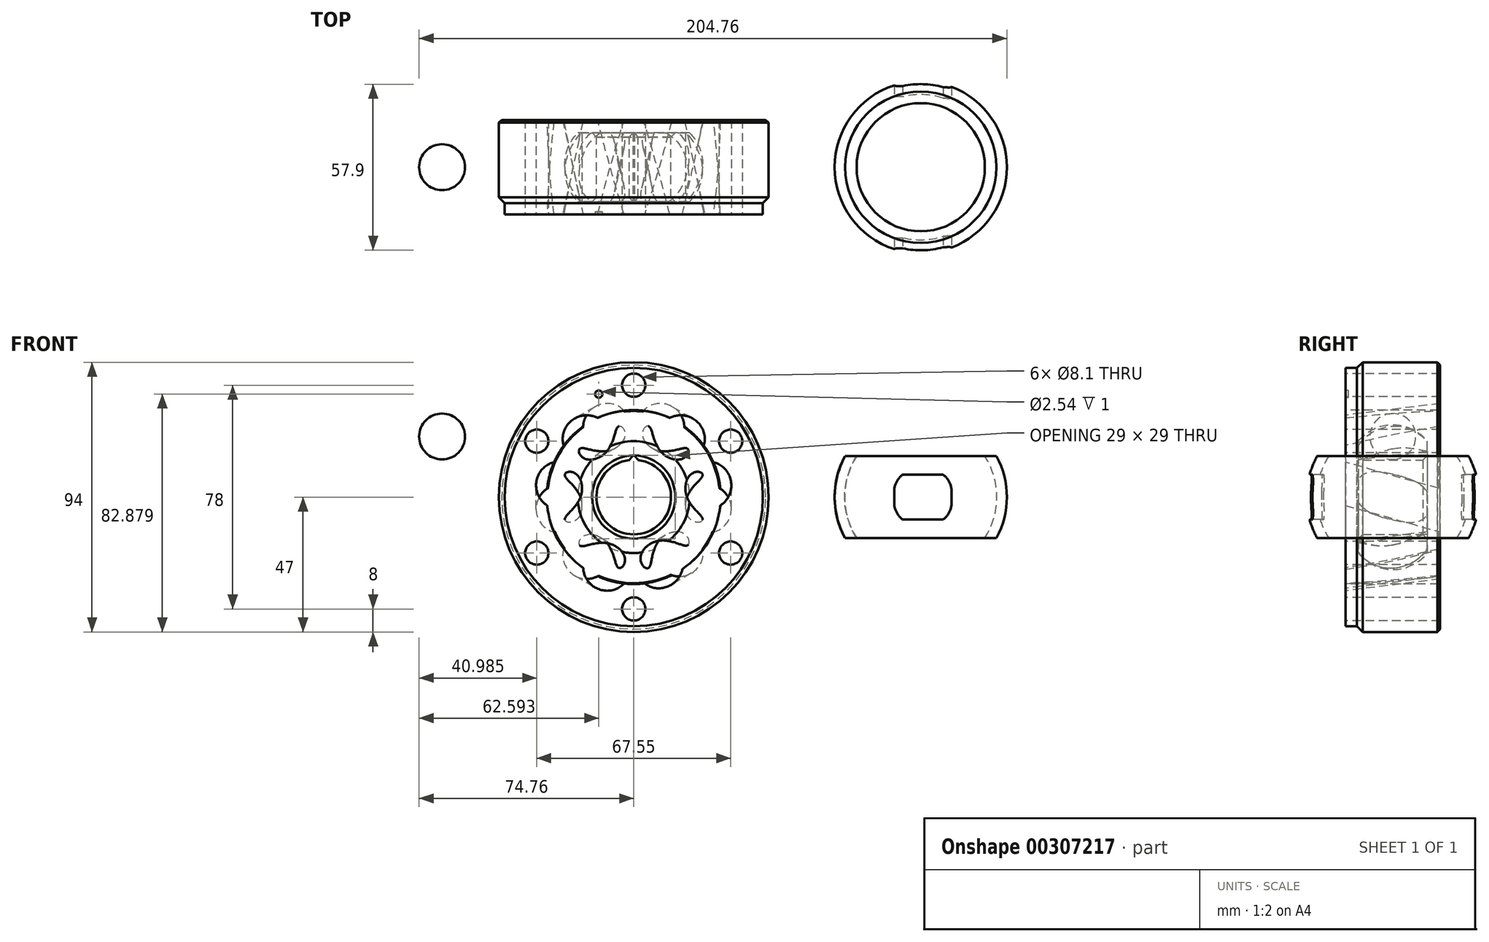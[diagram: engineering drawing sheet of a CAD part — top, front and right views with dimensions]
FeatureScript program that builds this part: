
annotation { "Feature Type Name" : "Feature", "Feature Type Description" : "" }
export const myFeature = defineFeature(function(context is Context, id is Id, definition is map)
    precondition{}
    {
        {
            var Q0;
            Q0=qCreatedBy(makeId("Front.planeOp"),FACE);
            var sketch = newSketch(context, id + "F0", { "sketchPlane" : qUnion([Q0])});
            skCircle(sketch, "E0", {"center": v(0, 0) * mm, "radius": 47 * mm});
            skSolve(sketch);
        }
        {
            var Q0;
            Q0 = qSketchRegion(id + "F0", true);
            extrude(context, id + "F1", {"entities" : qUnion([Q0]), "depth" : 33 * mm, "symmetric" : true});
        }
        {
            var Q0;
            Q0=qCreatedBy(makeId("Front.planeOp"),FACE);
            var sketch = newSketch(context, id + "F2", { "sketchPlane" : qUnion([Q0])});
            skCircle(sketch, "E1", {"center": v(0, 0) * mm, "radius": 39 * mm, "construction": true});
            skCircle(sketch, "E2", {"center": v(0, 39) * mm, "radius": 4.05 * mm});
            skCircle(sketch, "E3.1.1", {"center": v(-33.77, 19.5) * mm, "radius": 4.05 * mm});
            skCircle(sketch, "E3.2.1", {"center": v(-33.77, -19.5) * mm, "radius": 4.05 * mm});
            skCircle(sketch, "E3.3.1", {"center": v(0, -39) * mm, "radius": 4.05 * mm});
            skCircle(sketch, "E3.4.1", {"center": v(33.77, -19.5) * mm, "radius": 4.05 * mm});
            skCircle(sketch, "E3.5.1", {"center": v(33.77, 19.5) * mm, "radius": 4.05 * mm});
            skSolve(sketch);
        }
        {
            var Q0;
            Q0 = qSketchRegion(id + "F2", true);
            extrude(context, id + "F3", {"entities" : qUnion([Q0]), "operationType" : NewBodyOperationType.REMOVE, "oppositeDirection" : true, "depth" : 40 * mm, "symmetric" : true});
        }
        {
            var Q0;
            Q0=makeQuery(id+"F1.opExtrude","CAP_FACE",FACE,{"disambiguationData":[OSD([sQuery(id+"F0.wireOp",EDGE,"E0")])],"isStart":false});
            var sketch = newSketch(context, id + "F4", { "sketchPlane" : qUnion([Q0])});
            skCircle(sketch, "E4", {"center": v(0, 0) * mm, "radius": 30 * mm});
            skSolve(sketch);
        }
        {
            var Q0;
            Q0 = qSketchRegion(id + "F4", true);
            var Q1;
            Q1=makeQuery(id+"F1.opExtrude","CAP_FACE",FACE,{"disambiguationData":[OSD([sQuery(id+"F0.wireOp",EDGE,"E0")])],"isStart":true});
            extrude(context, id + "F5", {"entities" : qUnion([Q0]), "operationType" : NewBodyOperationType.REMOVE, "endBound" : BoundingType.UP_TO_SURFACE, "oppositeDirection" : true, "endBoundEntityFace" : qUnion([Q1]), "depth" : 25 * mm});
        }
        {
            var Q0;
            Q0=makeQuery(id+"F1.opExtrude","CAP_FACE",FACE,{"disambiguationData":[OSD([sQuery(id+"F0.wireOp",EDGE,"E0")])],"isStart":false});
            var sketch = newSketch(context, id + "F6", { "sketchPlane" : qUnion([Q0])});
            skCircle(sketch, "E5", {"center": v(0, 0) * mm, "radius": 45 * mm});
            skCircle(sketch, "E6", {"center": v(0, -1.7) * mm, "radius": 59.4 * mm});
            skSolve(sketch);
        }
        {
            var Q0;
            Q0 = qSketchRegion(id + "F6", true);
            extrude(context, id + "F7", {"entities" : qUnion([Q0]), "operationType" : NewBodyOperationType.REMOVE, "oppositeDirection" : true, "depth" : 6 * mm});
        }
        {
            var Q0;
            Q0=makeQuery(id+"F7.boolean.opBoolean","COPY",EDGE,{"derivedFrom":makeQuery(id+"F7.opExtrude","CAP_EDGE",EDGE,{"disambiguationData":[OSD([sQuery(id+"F6.wireOp",EDGE,"E5")])],"isStart":true})});
            var Q1;
            Q1=makeQuery(id+"F1.opExtrude","CAP_EDGE",EDGE,{"disambiguationData":[OSD([sQuery(id+"F0.wireOp",EDGE,"E0")])],"isStart":true});
            chamfer(context, id + "F8", {"entities" : qUnion([Q0, Q1]), "width" : 1 * mm, "tangentPropagation" : true});
        }
        {
            var Q0;
            Q0=makeQuery(id+"F7.boolean.opBoolean","COPY",EDGE,{"derivedFrom":makeQuery(id+"F7.opExtrude","CAP_EDGE",EDGE,{"disambiguationData":[OSD([sQuery(id+"F6.wireOp",EDGE,"E5")])],"isStart":false})});
            chamfer(context, id + "F9", {"entities" : qUnion([Q0]), "width" : 2 * mm, "tangentPropagation" : true});
        }
        {
            var Q0;
            Q0=qCreatedBy(makeId("Right.planeOp"),FACE);
            cPlane(context, id + "F10", {"entities" : qUnion([Q0]), "cplaneType" : CPlaneType.OFFSET, "offset" : 26 * mm, "width" : 150 * mm, "height" : 150 * mm});
        }
        {
            var Q0;
            Q0=qCreatedBy(id+"F10.planeOp",FACE);
            var sketch = newSketch(context, id + "F11", { "sketchPlane" : qUnion([Q0])});
            skLineSegment(sketch, "E7", {"start": v(45.9, 0) * mm, "end": v(-16.5, 0) * mm, "construction": true});
            skLineSegment(sketch, "E8", {"start": v(0, 0) * mm, "end": v(0, -57.5) * mm, "construction": true});
            skLineSegment(sketch, "E9", {"start": v(-16.5, 4.11) * mm, "end": v(16.5, -4.11) * mm, "construction": true});
            skLineSegment(sketch, "E10", {"start": v(0, 0) * mm, "end": v(-4.76, 1.19) * mm, "construction": true});
            skLineSegment(sketch, "E11", {"start": v(-16.5, 4.11) * mm, "end": v(-23.05, -22.17) * mm});
            skSolve(sketch);
        }
        {
            var Q0;
            Q0=sQuery(id+"F11.wireOp",EDGE,"E11");
            cPlane(context, id + "F12", {"entities" : qUnion([Q0]), "cplaneType" : CPlaneType.LINE_ANGLE, "offset" : 25 * mm, "angle" : 90 * degree, "oppositeDirection" : true, "width" : 150 * mm, "height" : 150 * mm});
        }
        {
            var Q0;
            Q0=qCreatedBy(id+"F12.planeOp",FACE);
            var sketch = newSketch(context, id + "F13", { "sketchPlane" : qUnion([Q0])});
            skCircle(sketch, "E12", {"center": v(26, 0) * mm, "radius": 8 * mm});
            skSolve(sketch);
        }
        {
            var Q0;
            Q0 = qSketchRegion(id + "F13", true);
            var Q1;
            Q1=makeQuery(id+"F1.opExtrude","CAP_FACE",FACE,{"disambiguationData":[OSD([sQuery(id+"F0.wireOp",EDGE,"E0")])],"isStart":true});
            extrude(context, id + "F14", {"entities" : qUnion([Q0]), "operationType" : NewBodyOperationType.REMOVE, "endBound" : BoundingType.UP_TO_SURFACE, "oppositeDirection" : true, "endBoundEntityFace" : qUnion([Q1]), "depth" : 25 * mm, "hasSecondDirection" : true, "secondDirectionOppositeDirection" : false, "secondDirectionDepth" : 25 * mm});
        }
        {
            var Q0;
            Q0=qCreatedBy(makeId("Top.planeOp"),FACE);
            var sketch = newSketch(context, id + "F15", { "sketchPlane" : qUnion([Q0])});
            skLineSegment(sketch, "E13", {"start": v(0, 0) * mm, "end": v(0, -105.8) * mm, "construction": true});
            skSolve(sketch);
        }
        {
            var Q0;
            Q0=sQuery(id+"F15.wireOp",EDGE,"E13");
            var Q1;
            Q1=qCreatedBy(makeId("Right.planeOp"),FACE);
            cPlane(context, id + "F16", {"entities" : qUnion([Q0, Q1]), "cplaneType" : CPlaneType.LINE_ANGLE, "offset" : 25 * mm, "angle" : 60 * degree, "width" : 150 * mm, "height" : 150 * mm});
        }
        {
            var Q0;
            Q0=qCreatedBy(id+"F16.planeOp",FACE);
            cPlane(context, id + "F17", {"entities" : qUnion([Q0]), "cplaneType" : CPlaneType.OFFSET, "offset" : 26 * mm, "width" : 150 * mm, "height" : 150 * mm});
        }
        {
            var Q0;
            Q0=sQuery(id+"F15.wireOp",EDGE,"E13");
            var Q1;
            Q1=qCreatedBy(makeId("Right.planeOp"),FACE);
            cPlane(context, id + "F18", {"entities" : qUnion([Q0, Q1]), "cplaneType" : CPlaneType.LINE_ANGLE, "offset" : 25 * mm, "angle" : 120 * degree, "width" : 150 * mm, "height" : 150 * mm});
        }
        {
            var Q0;
            Q0=qCreatedBy(id+"F18.planeOp",FACE);
            cPlane(context, id + "F19", {"entities" : qUnion([Q0]), "cplaneType" : CPlaneType.OFFSET, "offset" : 26 * mm, "oppositeDirection" : true, "width" : 150 * mm, "height" : 150 * mm});
        }
        {
            var Q0;
            Q0=qCreatedBy(id+"F19.planeOp",FACE);
            var sketch = newSketch(context, id + "F20", { "sketchPlane" : qUnion([Q0])});
            skLineSegment(sketch, "E14", {"start": v(0, 0) * mm, "end": v(0, 13.06) * mm, "construction": true});
            skLineSegment(sketch, "E15", {"start": v(0, 0) * mm, "end": v(-4.11, 16.5) * mm, "construction": true});
            skLineSegment(sketch, "E16", {"start": v(-4.11, 16.5) * mm, "end": v(37.61, 26.9) * mm, "construction": true});
            skSolve(sketch);
        }
        {
            var Q0;
            Q0=sQuery(id+"F20.wireOp",EDGE,"E16");
            var Q1;
            Q1=qCreatedBy(id+"F19.planeOp",FACE);
            cPlane(context, id + "F21", {"entities" : qUnion([Q0, Q1]), "cplaneType" : CPlaneType.LINE_ANGLE, "offset" : 25 * mm, "angle" : 90 * degree, "width" : 150 * mm, "height" : 150 * mm});
        }
        {
            var Q0;
            Q0=qCreatedBy(id+"F21.planeOp",FACE);
            var sketch = newSketch(context, id + "F22", { "sketchPlane" : qUnion([Q0])});
            skCircle(sketch, "E17", {"center": v(-13.3, 22.34) * mm, "radius": 8 * mm});
            skSolve(sketch);
        }
        {
            var Q0;
            Q0 = qSketchRegion(id + "F22", true);
            var Q1;
            Q1=makeQuery(id+"F1.opExtrude","CAP_FACE",FACE,{"disambiguationData":[OSD([sQuery(id+"F0.wireOp",EDGE,"E0")])],"isStart":true});
            var Q2;
            Q2=makeQuery(id+"F1.opExtrude","CAP_FACE",FACE,{"disambiguationData":[OSD([sQuery(id+"F0.wireOp",EDGE,"E0")])],"isStart":true});
            extrude(context, id + "F23", {"entities" : qUnion([Q0]), "operationType" : NewBodyOperationType.REMOVE, "endBound" : BoundingType.UP_TO_SURFACE, "oppositeDirection" : true, "endBoundEntityFace" : qUnion([Q1]), "depth" : 25 * mm, "hasSecondDirection" : true, "secondDirectionOppositeDirection" : false, "secondDirectionBoundEntityFace" : qUnion([Q2]), "secondDirectionDepth" : 25 * mm});
        }
        {
            var Q0;
            Q0=qCreatedBy(id+"F17.planeOp",FACE);
            var sketch = newSketch(context, id + "F24", { "sketchPlane" : qUnion([Q0])});
            skLineSegment(sketch, "E18", {"start": v(0, 0) * mm, "end": v(0, 11.58) * mm, "construction": true});
            skLineSegment(sketch, "E19", {"start": v(0, 0) * mm, "end": v(4.43, 17.75) * mm, "construction": true});
            skLineSegment(sketch, "E20", {"start": v(4.43, 17.75) * mm, "end": v(-28.29, 25.91) * mm, "construction": true});
            skSolve(sketch);
        }
        {
            var Q0;
            Q0=sQuery(id+"F24.wireOp",EDGE,"E20");
            var Q1;
            Q1=qCreatedBy(id+"F17.planeOp",FACE);
            cPlane(context, id + "F25", {"entities" : qUnion([Q0, Q1]), "cplaneType" : CPlaneType.LINE_ANGLE, "offset" : 25 * mm, "angle" : 90 * degree, "width" : 150 * mm, "height" : 150 * mm});
        }
        {
            var Q0;
            Q0=qCreatedBy(id+"F25.planeOp",FACE);
            var sketch = newSketch(context, id + "F26", { "sketchPlane" : qUnion([Q0])});
            skCircle(sketch, "E21", {"center": v(13.3, -22.34) * mm, "radius": 8 * mm});
            skSolve(sketch);
        }
        {
            var Q0;
            Q0 = qSketchRegion(id + "F26", true);
            var Q1;
            Q1=makeQuery(id+"F1.opExtrude","CAP_FACE",FACE,{"disambiguationData":[OSD([sQuery(id+"F0.wireOp",EDGE,"E0")])],"isStart":true});
            extrude(context, id + "F27", {"entities" : qUnion([Q0]), "operationType" : NewBodyOperationType.REMOVE, "endBound" : BoundingType.UP_TO_SURFACE, "endBoundEntityFace" : qUnion([Q1]), "depth" : 25 * mm, "hasSecondDirection" : true, "secondDirectionOppositeDirection" : true, "secondDirectionDepth" : 25 * mm});
        }
        {
            var Q0;
            Q0=qCreatedBy(makeId("Top.planeOp"),FACE);
            var Q1;
            Q1=sQuery(id+"F15.wireOp",EDGE,"E13");
            cPlane(context, id + "F28", {"entities" : qUnion([Q0, Q1]), "cplaneType" : CPlaneType.LINE_ANGLE, "offset" : 25 * mm, "angle" : 330 * degree, "width" : 150 * mm, "height" : 150 * mm});
        }
        {
            var Q0;
            Q0=qCreatedBy(id+"F28.planeOp",FACE);
            cPlane(context, id + "F29", {"entities" : qUnion([Q0]), "cplaneType" : CPlaneType.OFFSET, "offset" : 26 * mm, "oppositeDirection" : true, "width" : 150 * mm, "height" : 150 * mm});
        }
        {
            var Q0;
            Q0=qCreatedBy(id+"F29.planeOp",FACE);
            var sketch = newSketch(context, id + "F30", { "sketchPlane" : qUnion([Q0])});
            skLineSegment(sketch, "E22", {"start": v(0, 0) * mm, "end": v(0, 16.49) * mm, "construction": true});
            skLineSegment(sketch, "E23", {"start": v(0, 0) * mm, "end": v(4.76, 19.08) * mm, "construction": true});
            skLineSegment(sketch, "E24", {"start": v(4.76, 19.08) * mm, "end": v(-15.36, 24.1) * mm, "construction": true});
            skSolve(sketch);
        }
        {
            var Q0;
            Q0=sQuery(id+"F30.wireOp",EDGE,"E24");
            var Q1;
            Q1=qCreatedBy(id+"F29.planeOp",FACE);
            cPlane(context, id + "F31", {"entities" : qUnion([Q0, Q1]), "cplaneType" : CPlaneType.LINE_ANGLE, "offset" : 25 * mm, "angle" : 90 * degree, "width" : 150 * mm, "height" : 150 * mm});
        }
        {
            var Q0;
            Q0=qCreatedBy(id+"F31.planeOp",FACE);
            var sketch = newSketch(context, id + "F32", { "sketchPlane" : qUnion([Q0])});
            skCircle(sketch, "E25", {"center": v(-13.3, 22.34) * mm, "radius": 8 * mm});
            skSolve(sketch);
        }
        {
            var Q0;
            Q0 = qSketchRegion(id + "F32", true);
            var Q1;
            Q1=makeQuery(id+"F1.opExtrude","CAP_FACE",FACE,{"disambiguationData":[OSD([sQuery(id+"F0.wireOp",EDGE,"E0")])],"isStart":true});
            extrude(context, id + "F33", {"entities" : qUnion([Q0]), "operationType" : NewBodyOperationType.REMOVE, "endBound" : BoundingType.UP_TO_SURFACE, "endBoundEntityFace" : qUnion([Q1]), "depth" : 25 * mm});
        }
        {
            var Q0;
            Q0=sQuery(id+"F15.wireOp",EDGE,"E13");
            var Q1;
            Q1=qCreatedBy(id+"F28.planeOp",FACE);
            cPlane(context, id + "F34", {"entities" : qUnion([Q0, Q1]), "cplaneType" : CPlaneType.LINE_ANGLE, "offset" : 25 * mm, "angle" : 120 * degree, "width" : 150 * mm, "height" : 150 * mm});
        }
        {
            var Q0;
            Q0=qCreatedBy(id+"F34.planeOp",FACE);
            cPlane(context, id + "F35", {"entities" : qUnion([Q0]), "cplaneType" : CPlaneType.OFFSET, "offset" : 26 * mm, "width" : 150 * mm, "height" : 150 * mm});
        }
        {
            var Q0;
            Q0=qCreatedBy(id+"F35.planeOp",FACE);
            var sketch = newSketch(context, id + "F36", { "sketchPlane" : qUnion([Q0])});
            skLineSegment(sketch, "E26", {"start": v(0, 0) * mm, "end": v(13.95, 0) * mm, "construction": true});
            skLineSegment(sketch, "E27", {"start": v(0, 0) * mm, "end": v(16.5, 4.11) * mm, "construction": true});
            skLineSegment(sketch, "E28", {"start": v(16.5, 4.11) * mm, "end": v(20.29, -11.07) * mm, "construction": true});
            skSolve(sketch);
        }
        {
            var Q0;
            Q0=sQuery(id+"F36.wireOp",EDGE,"E28");
            var Q1;
            Q1=qCreatedBy(id+"F35.planeOp",FACE);
            cPlane(context, id + "F37", {"entities" : qUnion([Q0, Q1]), "cplaneType" : CPlaneType.LINE_ANGLE, "offset" : 25 * mm, "angle" : 90 * degree, "width" : 150 * mm, "height" : 150 * mm});
        }
        {
            var Q0;
            Q0=qCreatedBy(id+"F37.planeOp",FACE);
            var sketch = newSketch(context, id + "F38", { "sketchPlane" : qUnion([Q0])});
            skCircle(sketch, "E29", {"center": v(-26, 0) * mm, "radius": 8 * mm});
            skSolve(sketch);
        }
        {
            var Q0;
            Q0 = qSketchRegion(id + "F38", true);
            var Q1;
            Q1=makeQuery(id+"F1.opExtrude","CAP_FACE",FACE,{"disambiguationData":[OSD([sQuery(id+"F0.wireOp",EDGE,"E0")])],"isStart":true});
            extrude(context, id + "F39", {"entities" : qUnion([Q0]), "operationType" : NewBodyOperationType.REMOVE, "endBound" : BoundingType.UP_TO_SURFACE, "oppositeDirection" : true, "endBoundEntityFace" : qUnion([Q1]), "depth" : 25 * mm, "hasSecondDirection" : true, "secondDirectionOppositeDirection" : false, "secondDirectionDepth" : 25 * mm});
        }
        {
            var Q0;
            Q0=qCreatedBy(id+"F34.planeOp",FACE);
            var Q1;
            Q1=sQuery(id+"F15.wireOp",EDGE,"E13");
            cPlane(context, id + "F40", {"entities" : qUnion([Q0, Q1]), "cplaneType" : CPlaneType.LINE_ANGLE, "offset" : 25 * mm, "angle" : 120 * degree, "width" : 150 * mm, "height" : 150 * mm});
        }
        {
            var Q0;
            Q0=qCreatedBy(id+"F40.planeOp",FACE);
            cPlane(context, id + "F41", {"entities" : qUnion([Q0]), "cplaneType" : CPlaneType.OFFSET, "offset" : 25 * mm, "oppositeDirection" : true, "width" : 150 * mm, "height" : 150 * mm});
        }
        {
            var Q0;
            Q0=qCreatedBy(id+"F41.planeOp",FACE);
            var sketch = newSketch(context, id + "F42", { "sketchPlane" : qUnion([Q0])});
            skLineSegment(sketch, "E30", {"start": v(0, 0) * mm, "end": v(0, -15.94) * mm, "construction": true});
            skLineSegment(sketch, "E31", {"start": v(0, 0) * mm, "end": v(-4.11, -16.5) * mm, "construction": true});
            skLineSegment(sketch, "E32", {"start": v(-4.11, -16.5) * mm, "end": v(10.82, -20.22) * mm, "construction": true});
            skSolve(sketch);
        }
        {
            var Q0;
            Q0=sQuery(id+"F42.wireOp",EDGE,"E32");
            var Q1;
            Q1=qCreatedBy(id+"F41.planeOp",FACE);
            cPlane(context, id + "F43", {"entities" : qUnion([Q0, Q1]), "cplaneType" : CPlaneType.LINE_ANGLE, "offset" : 25 * mm, "angle" : 90 * degree, "width" : 150 * mm, "height" : 150 * mm});
        }
        {
            var Q0;
            Q0=qCreatedBy(id+"F43.planeOp",FACE);
            var sketch = newSketch(context, id + "F44", { "sketchPlane" : qUnion([Q0])});
            skCircle(sketch, "E33", {"center": v(-12.78, -21.48) * mm, "radius": 8 * mm});
            skSolve(sketch);
        }
        {
            var Q0;
            Q0 = qSketchRegion(id + "F44", true);
            var Q1;
            Q1=makeQuery(id+"F1.opExtrude","CAP_FACE",FACE,{"disambiguationData":[OSD([sQuery(id+"F0.wireOp",EDGE,"E0")])],"isStart":true});
            extrude(context, id + "F45", {"entities" : qUnion([Q0]), "operationType" : NewBodyOperationType.REMOVE, "endBound" : BoundingType.UP_TO_SURFACE, "endBoundEntityFace" : qUnion([Q1]), "depth" : 25 * mm, "hasSecondDirection" : true, "secondDirectionOppositeDirection" : true, "secondDirectionDepth" : 25 * mm});
        }
        {
            var Q0;
            Q0=qCreatedBy(makeId("Front.planeOp"),FACE);
            var sketch = newSketch(context, id + "F46", { "sketchPlane" : qUnion([Q0])});
            skArc(sketch, "E34", {"start": v(-66.76, 29.11) * mm, "mid": v(-74.76, 21.11) * mm, "end": v(-66.76, 13.11) * mm});
            skLineSegment(sketch, "E35", {"start": v(-66.76, 29.11) * mm, "end": v(-66.76, 13.11) * mm});
            skLineSegment(sketch, "E36", {"start": v(-66.76, 42.78) * mm, "end": v(-66.76, -5.2) * mm, "construction": true});
            skSolve(sketch);
        }
        {
            var Q0;
            Q0 = qSketchRegion(id + "F46", true);
            var Q1;
            Q1=sQuery(id+"F46.wireOp",EDGE,"E35");
            revolve(context, id + "F47", {"entities" : qUnion([Q0]), "axis" : qUnion([Q1]), "revolveType" : RevolveType.FULL});
        }
        {
            var Q0;
            Q0=qCreatedBy(makeId("Right.planeOp"),FACE);
            cPlane(context, id + "F48", {"entities" : qUnion([Q0]), "cplaneType" : CPlaneType.OFFSET, "offset" : 100 * mm, "width" : 150 * mm, "height" : 150 * mm});
        }
        {
            var Q0;
            Q0=qCreatedBy(makeId("Front.planeOp"),FACE);
            var sketch = newSketch(context, id + "F49", { "sketchPlane" : qUnion([Q0])});
            skArc(sketch, "E37", {"start": v(100, -30) * mm, "mid": v(130, 0) * mm, "end": v(100, 30) * mm});
            skLineSegment(sketch, "E38", {"start": v(100, 30) * mm, "end": v(100, -30) * mm});
            skSolve(sketch);
        }
        {
            var Q0;
            Q0 = qSketchRegion(id + "F49", true);
            var Q1;
            Q1=sQuery(id+"F49.wireOp",EDGE,"E38");
            revolve(context, id + "F50", {"entities" : qUnion([Q0]), "axis" : qUnion([Q1]), "revolveType" : RevolveType.FULL});
        }
        {
            var Q0;
            Q0=qCreatedBy(makeId("Front.planeOp"),FACE);
            var sketch = newSketch(context, id + "F51", { "sketchPlane" : qUnion([Q0])});
            skLineSegment(sketch, "E39", {"start": v(65.97, 0) * mm, "end": v(144.14, 0) * mm, "construction": true});
            skLineSegment(sketch, "E40.bottom", {"start": v(66.97, -14.25) * mm, "end": v(140.64, -14.25) * mm});
            skLineSegment(sketch, "E40.top", {"start": v(66.97, -42.47) * mm, "end": v(140.64, -42.47) * mm});
            skLineSegment(sketch, "E40.left", {"start": v(66.97, -14.25) * mm, "end": v(66.97, -42.47) * mm});
            skLineSegment(sketch, "E40.right", {"start": v(140.64, -14.25) * mm, "end": v(140.64, -42.47) * mm});
            skLineSegment(sketch, "E41.bottom", {"start": v(66.97, 14.25) * mm, "end": v(140.64, 14.25) * mm});
            skLineSegment(sketch, "E41.top", {"start": v(66.97, 36.05) * mm, "end": v(140.64, 36.05) * mm});
            skLineSegment(sketch, "E41.left", {"start": v(66.97, 14.25) * mm, "end": v(66.97, 36.05) * mm});
            skLineSegment(sketch, "E41.right", {"start": v(140.64, 14.25) * mm, "end": v(140.64, 36.05) * mm});
            skSolve(sketch);
        }
        {
            var Q0;
            Q0 = qSketchRegion(id + "F51", true);
            extrude(context, id + "F52", {"entities" : qUnion([Q0]), "operationType" : NewBodyOperationType.REMOVE, "oppositeDirection" : true, "depth" : 100 * mm, "symmetric" : true});
        }
        {
            var Q0;
            Q0=makeQuery(id+"F52.boolean.opBoolean","COPY",FACE,{"derivedFrom":makeQuery(id+"F52.opExtrude","SWEPT_FACE",FACE,{"disambiguationData":[OSD([sQuery(id+"F51.wireOp",EDGE,"E41.bottom")])]})});
            var Q1;
            Q1=makeQuery(id+"F52.boolean.opBoolean","COPY",FACE,{"derivedFrom":makeQuery(id+"F52.opExtrude","SWEPT_FACE",FACE,{"disambiguationData":[OSD([sQuery(id+"F51.wireOp",EDGE,"E40.bottom")])]})});
            shell(context, id + "F53", {"entities" : qUnion([Q0, Q1]), "thickness" : 3.5 * mm});
        }
        {
            var Q0;
            Q0=qCreatedBy(makeId("Front.planeOp"),FACE);
            var sketch = newSketch(context, id + "F54", { "sketchPlane" : qUnion([Q0])});
            skLineSegment(sketch, "E42.bottom", {"start": v(107.75, -7.85) * mm, "end": v(93.75, -7.85) * mm});
            skLineSegment(sketch, "E42.top", {"start": v(107.75, 7.85) * mm, "end": v(93.75, 7.85) * mm});
            skLineSegment(sketch, "E42.left", {"start": v(110.75, -2) * mm, "end": v(110.75, 2) * mm});
            skLineSegment(sketch, "E42.right", {"start": v(90.75, -2) * mm, "end": v(90.75, 2) * mm});
            skPoint(sketch, "E42.middle", {"position": v(100.75, 0) * mm});
            skPoint(sketch, "E43.middle", {"position": v(99.82, -11.86) * mm});
            skLineSegment(sketch, "E44", {"start": v(93.75, 7.85) * mm, "end": v(93.75, -7.85) * mm, "construction": true});
            skLineSegment(sketch, "E45", {"start": v(107.75, 7.85) * mm, "end": v(107.75, -7.85) * mm, "construction": true});
            skLineSegment(sketch, "E46", {"start": v(90.75, 2) * mm, "end": v(110.75, 2) * mm, "construction": true});
            skLineSegment(sketch, "E47", {"start": v(110.75, -2) * mm, "end": v(90.75, -2) * mm, "construction": true});
            skLineSegment(sketch, "E48", {"start": v(100.75, 0) * mm, "end": v(103.88, 0) * mm, "construction": true});
            skArc(sketch, "E49", {"start": v(110.75, 2) * mm, "mid": v(109.96, 5.29) * mm, "end": v(107.75, 7.85) * mm});
            skArc(sketch, "E50", {"start": v(107.75, -7.85) * mm, "mid": v(109.96, -5.29) * mm, "end": v(110.75, -2) * mm});
            skArc(sketch, "E51", {"start": v(90.75, -2) * mm, "mid": v(91.55, -5.29) * mm, "end": v(93.75, -7.85) * mm});
            skArc(sketch, "E52", {"start": v(93.75, 7.85) * mm, "mid": v(91.55, 5.29) * mm, "end": v(90.75, 2) * mm});
            skPoint(sketch, "E53.orphan", {"position": v(90.75, 7.85) * mm});
            skPoint(sketch, "E54.orphan", {"position": v(90.75, -7.85) * mm});
            skPoint(sketch, "E55.orphan", {"position": v(110.75, -7.85) * mm});
            skPoint(sketch, "E56.orphan", {"position": v(110.75, 7.85) * mm});
            skSolve(sketch);
        }
        {
            var Q0;
            Q0 = qSketchRegion(id + "F54", true);
            extrude(context, id + "F55", {"entities" : qUnion([Q0]), "operationType" : NewBodyOperationType.REMOVE, "oppositeDirection" : true, "depth" : 70 * mm, "symmetric" : true});
        }
        {
            var Q0;
            Q0=qCreatedBy(makeId("Front.planeOp"),FACE);
            var sketch = newSketch(context, id + "F56", { "sketchPlane" : qUnion([Q0])});
            skCircle(sketch, "E57", {"center": v(0, 0) * mm, "radius": 25.25 * mm});
            skCircle(sketch, "E58", {"center": v(0, 0) * mm, "radius": 14.5 * mm, "construction": true});
            skCircle(sketch, "E59", {"center": v(0, 0) * mm, "radius": 13 * mm});
            skSolve(sketch);
        }
        {
            var Q0;
            Q0 = qSketchRegion(id + "F56", true);
            extrude(context, id + "F57", {"entities" : qUnion([Q0]), "depth" : 24 * mm, "symmetric" : true});
        }
        {
            var Q0;
            Q0=qCreatedBy(id+"F10.planeOp",FACE);
            var sketch = newSketch(context, id + "F58", { "sketchPlane" : qUnion([Q0])});
            skLineSegment(sketch, "E60", {"start": v(0, 0) * mm, "end": v(-16.5, 0) * mm});
            skLineSegment(sketch, "E61", {"start": v(0, 0) * mm, "end": v(-16.5, 4.11) * mm});
            skSolve(sketch);
        }
        {
            var Q0;
            Q0=qCreatedBy(id+"F12.planeOp",FACE);
            var sketch = newSketch(context, id + "F59", { "sketchPlane" : qUnion([Q0])});
            skCircle(sketch, "E62", {"center": v(26, 0) * mm, "radius": 8 * mm});
            skSolve(sketch);
        }
        {
            var Q0;
            Q0 = qSketchRegion(id + "F59", true);
            var Q1;
            Q1=makeQuery(id+"F57.opExtrude","CAP_FACE",FACE,{"disambiguationData":[OSD([sQuery(id+"F56.wireOp",EDGE,"E57"),sQuery(id+"F56.wireOp",EDGE,"E58")])],"isStart":true});
            extrude(context, id + "F60", {"entities" : qUnion([Q0]), "operationType" : NewBodyOperationType.REMOVE, "endBound" : BoundingType.UP_TO_SURFACE, "oppositeDirection" : true, "endBoundEntityFace" : qUnion([Q1]), "depth" : 25 * mm});
        }
        {
            var Q0;
            Q0=qCreatedBy(id+"F19.planeOp",FACE);
            var sketch = newSketch(context, id + "F61", { "sketchPlane" : qUnion([Q0])});
            skLineSegment(sketch, "E63", {"start": v(0, 0) * mm, "end": v(0, 7.15) * mm});
            skLineSegment(sketch, "E64", {"start": v(0, 0) * mm, "end": v(-4.11, 16.5) * mm});
            skSolve(sketch);
        }
        {
            var Q0;
            Q0=qCreatedBy(id+"F21.planeOp",FACE);
            var sketch = newSketch(context, id + "F62", { "sketchPlane" : qUnion([Q0])});
            skCircle(sketch, "E65", {"center": v(-13.3, 22.34) * mm, "radius": 8 * mm});
            skSolve(sketch);
        }
        {
            var Q0;
            Q0 = qSketchRegion(id + "F62", true);
            var Q1;
            Q1=makeQuery(id+"F57.opExtrude","CAP_FACE",FACE,{"disambiguationData":[OSD([sQuery(id+"F56.wireOp",EDGE,"E57"),sQuery(id+"F56.wireOp",EDGE,"E58")])],"isStart":true});
            extrude(context, id + "F63", {"entities" : qUnion([Q0]), "operationType" : NewBodyOperationType.REMOVE, "endBound" : BoundingType.UP_TO_SURFACE, "oppositeDirection" : true, "endBoundEntityFace" : qUnion([Q1]), "depth" : 25 * mm});
        }
        {
            var Q0;
            Q0=qCreatedBy(id+"F17.planeOp",FACE);
            var sketch = newSketch(context, id + "F64", { "sketchPlane" : qUnion([Q0])});
            skLineSegment(sketch, "E66", {"start": v(0, 0) * mm, "end": v(0, 9.52) * mm});
            skLineSegment(sketch, "E67", {"start": v(0, 0) * mm, "end": v(4.43, 17.75) * mm});
            skSolve(sketch);
        }
        {
            var Q0;
            Q0=qCreatedBy(id+"F25.planeOp",FACE);
            var sketch = newSketch(context, id + "F65", { "sketchPlane" : qUnion([Q0])});
            skCircle(sketch, "E68", {"center": v(13.3, -22.34) * mm, "radius": 8 * mm});
            skSolve(sketch);
        }
        {
            var Q0;
            Q0=qCreatedBy(id+"F29.planeOp",FACE);
            var sketch = newSketch(context, id + "F66", { "sketchPlane" : qUnion([Q0])});
            skLineSegment(sketch, "E69", {"start": v(0, 0) * mm, "end": v(0, 7.14) * mm});
            skLineSegment(sketch, "E70", {"start": v(0, 0) * mm, "end": v(4.76, 19.08) * mm});
            skSolve(sketch);
        }
        {
            var Q0;
            Q0=qCreatedBy(id+"F31.planeOp",FACE);
            var sketch = newSketch(context, id + "F67", { "sketchPlane" : qUnion([Q0])});
            skCircle(sketch, "E71", {"center": v(-13.3, 22.34) * mm, "radius": 8 * mm});
            skSolve(sketch);
        }
        {
            var Q0;
            Q0 = qSketchRegion(id + "F67", true);
            var Q1;
            Q1=makeQuery(id+"F57.opExtrude","CAP_FACE",FACE,{"disambiguationData":[OSD([sQuery(id+"F56.wireOp",EDGE,"E57"),sQuery(id+"F56.wireOp",EDGE,"E58")])],"isStart":true});
            extrude(context, id + "F68", {"entities" : qUnion([Q0]), "operationType" : NewBodyOperationType.REMOVE, "endBound" : BoundingType.UP_TO_SURFACE, "endBoundEntityFace" : qUnion([Q1]), "depth" : 25 * mm});
        }
        {
            var Q0;
            Q0=qCreatedBy(id+"F35.planeOp",FACE);
            var sketch = newSketch(context, id + "F69", { "sketchPlane" : qUnion([Q0])});
            skLineSegment(sketch, "E72", {"start": v(0, 0) * mm, "end": v(9.7, 0) * mm});
            skLineSegment(sketch, "E73", {"start": v(0, 0) * mm, "end": v(16.5, 4.11) * mm});
            skSolve(sketch);
        }
        {
            var Q0;
            Q0=qCreatedBy(id+"F37.planeOp",FACE);
            var sketch = newSketch(context, id + "F70", { "sketchPlane" : qUnion([Q0])});
            skCircle(sketch, "E74", {"center": v(-26, 0) * mm, "radius": 8 * mm});
            skSolve(sketch);
        }
        {
            var Q0;
            Q0 = qSketchRegion(id + "F70", true);
            var Q1;
            Q1=makeQuery(id+"F57.opExtrude","CAP_FACE",FACE,{"disambiguationData":[OSD([sQuery(id+"F56.wireOp",EDGE,"E57"),sQuery(id+"F56.wireOp",EDGE,"E58")])],"isStart":true});
            extrude(context, id + "F71", {"entities" : qUnion([Q0]), "operationType" : NewBodyOperationType.REMOVE, "endBound" : BoundingType.UP_TO_SURFACE, "oppositeDirection" : true, "endBoundEntityFace" : qUnion([Q1]), "depth" : 25 * mm});
        }
        {
            var Q0;
            Q0=qCreatedBy(id+"F41.planeOp",FACE);
            var sketch = newSketch(context, id + "F72", { "sketchPlane" : qUnion([Q0])});
            skLineSegment(sketch, "E75", {"start": v(0, 0) * mm, "end": v(0, -9.09) * mm});
            skLineSegment(sketch, "E76", {"start": v(0, 0) * mm, "end": v(-4.11, -16.5) * mm});
            skSolve(sketch);
        }
        {
            var Q0;
            Q0=qCreatedBy(id+"F43.planeOp",FACE);
            var sketch = newSketch(context, id + "F73", { "sketchPlane" : qUnion([Q0])});
            skCircle(sketch, "E77", {"center": v(-12.78, -21.48) * mm, "radius": 8 * mm});
            skSolve(sketch);
        }
        {
            var Q0;
            Q0 = qSketchRegion(id + "F73", true);
            var Q1;
            Q1=makeQuery(id+"F57.opExtrude","CAP_FACE",FACE,{"disambiguationData":[OSD([sQuery(id+"F56.wireOp",EDGE,"E57"),sQuery(id+"F56.wireOp",EDGE,"E58")])],"isStart":true});
            extrude(context, id + "F74", {"entities" : qUnion([Q0]), "operationType" : NewBodyOperationType.REMOVE, "endBound" : BoundingType.UP_TO_SURFACE, "endBoundEntityFace" : qUnion([Q1]), "depth" : 25 * mm});
        }
        {
            var Q0;
            Q0=qCreatedBy(makeId("Top.planeOp"),FACE);
            var sketch = newSketch(context, id + "F75", { "sketchPlane" : qUnion([Q0])});
            skLineSegment(sketch, "E78", {"start": v(0, 0) * mm, "end": v(40.15, 0) * mm, "construction": true});
            skLineSegment(sketch, "E79", {"start": v(0, 0) * mm, "end": v(0, -30.92) * mm, "construction": true});
            skArc(sketch, "E80", {"start": v(-19.5, 12) * mm, "mid": v(-23.73, 6.65) * mm, "end": v(-25.25, 0) * mm});
            skArc(sketch, "E81", {"start": v(-25.25, 0) * mm, "mid": v(-23.73, -6.65) * mm, "end": v(-19.5, -12) * mm});
            skLineSegment(sketch, "E82", {"start": v(-30.3, 15.96) * mm, "end": v(-30.3, -19.54) * mm});
            skLineSegment(sketch, "E83", {"start": v(-30.3, -19.54) * mm, "end": v(-19.5, -12) * mm});
            skLineSegment(sketch, "E84", {"start": v(-19.5, 12) * mm, "end": v(-30.3, 15.96) * mm});
            skSolve(sketch);
        }
        {
            var Q0;
            Q0=makeQuery(id+"F1.opExtrude","CAP_FACE",FACE,{"disambiguationData":[OSD([sQuery(id+"F0.wireOp",EDGE,"E0")])],"isStart":false});
            var sketch = newSketch(context, id + "F76", { "sketchPlane" : qUnion([Q0])});
            skCircle(sketch, "E85", {"center": v(-12.17, 35.88) * mm, "radius": 1.27 * mm});
            skSolve(sketch);
        }
        {
            var Q0;
            Q0 = qSketchRegion(id + "F76", true);
            extrude(context, id + "F77", {"entities" : qUnion([Q0]), "operationType" : NewBodyOperationType.REMOVE, "oppositeDirection" : true, "depth" : 1 * mm});
        }
        {
            var Q0;
            Q0=makeQuery(id+"F57.opExtrude","CAP_FACE",FACE,{"disambiguationData":[OSD([sQuery(id+"F56.wireOp",EDGE,"E57"),sQuery(id+"F56.wireOp",EDGE,"E58")])],"isStart":false});
            var sketch = newSketch(context, id + "F78", { "sketchPlane" : qUnion([Q0])});
            skCircle(sketch, "E86", {"center": v(-4.57, 21.78) * mm, "radius": 1.43 * mm});
            skSolve(sketch);
        }
        {
            var Q0;
            Q0 = qSketchRegion(id + "F78", true);
            extrude(context, id + "F79", {"entities" : qUnion([Q0]), "operationType" : NewBodyOperationType.REMOVE, "oppositeDirection" : true, "depth" : 1 * mm});
        }
        {
            var Q0;
            Q0 = qSketchRegion(id + "F65", true);
            var Q1;
            Q1=makeQuery(id+"F57.opExtrude","CAP_FACE",FACE,{"disambiguationData":[OSD([sQuery(id+"F56.wireOp",EDGE,"E57"),sQuery(id+"F56.wireOp",EDGE,"E58")])],"isStart":true});
            extrude(context, id + "F80", {"entities" : qUnion([Q0]), "operationType" : NewBodyOperationType.REMOVE, "endBound" : BoundingType.UP_TO_SURFACE, "endBoundEntityFace" : qUnion([Q1]), "depth" : 25 * mm});
        }
        {
            var Q0;
            Q0 = qSketchRegion(id + "F75", true);
            var Q1;
            Q1=sQuery(id+"F75.wireOp",EDGE,"E79");
            revolve(context, id + "F81", {"operationType" : NewBodyOperationType.REMOVE, "entities" : qUnion([Q0]), "axis" : qUnion([Q1]), "revolveType" : RevolveType.FULL, "oppositeDirection" : true});
        }
        {
            var Q0;
            Q0=makeQuery(id+"F57.opExtrude","SWEPT_FACE",FACE,{"disambiguationData":[OSD([sQuery(id+"F56.wireOp",EDGE,"E59")])]});
            chamfer(context, id + "F82", {"entities" : qUnion([Q0]), "width" : 1.5 * mm, "tangentPropagation" : true});
        }
        {
            var Q0;
            Q0=makeQuery(id+"F57.opExtrude","CAP_FACE",FACE,{"disambiguationData":[OSD([sQuery(id+"F56.wireOp",EDGE,"E57"),sQuery(id+"F56.wireOp",EDGE,"E59")])],"isStart":false});
            var sketch = newSketch(context, id + "F83", { "sketchPlane" : qUnion([Q0])});
            skLineSegment(sketch, "E87", {"start": v(0, 14.5) * mm, "end": v(0, 12.8) * mm, "construction": true});
            skLineSegment(sketch, "E88", {"start": v(0, 12.8) * mm, "end": v(1.65, 12.8) * mm});
            skLineSegment(sketch, "E89", {"start": v(1.65, 12.8) * mm, "end": v(0.25, 14.5) * mm});
            skLineSegment(sketch, "E90", {"start": v(0, 12.8) * mm, "end": v(-1.65, 12.8) * mm});
            skLineSegment(sketch, "E91", {"start": v(-1.65, 12.8) * mm, "end": v(-0.25, 14.5) * mm});
            skArc(sketch, "E92", {"start": v(-0.25, 14.5) * mm, "mid": v(0, 14.5) * mm, "end": v(0.25, 14.5) * mm});
            skLineSegment(sketch, "E93", {"start": v(0, 12.8) * mm, "end": v(0, 0) * mm, "construction": true});
            skSolve(sketch);
        }
        {
            var Q0;
            Q0 = qSketchRegion(id + "F83", true);
            var Q1;
            Q1=makeQuery(id+"F57.opExtrude","CAP_FACE",FACE,{"disambiguationData":[OSD([sQuery(id+"F56.wireOp",EDGE,"E57"),sQuery(id+"F56.wireOp",EDGE,"E59")])],"isStart":true});
            extrude(context, id + "F84", {"entities" : qUnion([Q0]), "operationType" : NewBodyOperationType.REMOVE, "endBound" : BoundingType.UP_TO_SURFACE, "oppositeDirection" : true, "endBoundEntityFace" : qUnion([Q1]), "depth" : 25 * mm});
        }
    });
